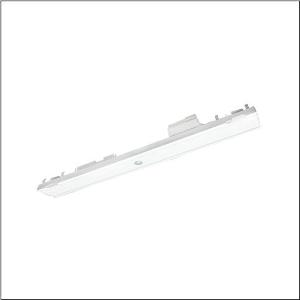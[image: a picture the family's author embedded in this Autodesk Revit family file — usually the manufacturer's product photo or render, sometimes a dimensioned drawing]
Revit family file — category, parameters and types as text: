
# Revit family: licross_r_56tl157c4x31_efa4
name_source: partatom
category: Lighting Fixtures
units: mm (PartAtom-declared; Revit-internal decimal feet)

## family parameters
Cut with Voids When Loaded = No
Host = Face
Light Source = No
Part Type = Normal
Room Calculation Point = No
Round Connector Dimension = Use Diameter
Shared = No

## types (1)
- Licross® (1 x LED, 320 lm, 3.9 W, 4000K)
    Apparent Load = 4 VA
    CIE Flux Codes = 31 68 99 100 100
    Color Rendering = 70
    Color Temperature = 4000K
    Default Elevation = 1800 mm
    Description = Licross®, luminaire insert, of sheet steel, coil coated, white, length: 500mm, width: 59mm, height: 60mm, mounting height: 2.5..7m, emergency light element,LED rated luminous flux: 320lm, light colour: 740, control gear: CEAG, with plug, 6-pole, with phase selection, mains connection: 220..240V, AC/DC, 0/50..60Hz, rated input power: 3.9W, halogen-free wiring, for trunking rail, 9..14-pole, for emergency light function, supply monitoring module CEAG, with address switch, choice between two emergency light lines via tool-free moving of contact pin prior to installation in trunking rail, primary light control with lens, of PMMA, primary optical cover: cover, of PMMA, light emission: direct distribution, primary light characteristic: symmetric,  for area, compatible with all CEAG STAR technology systems (ZB-S, DG-S (DualGuard-S), LP-STAR, AT-S+), protection rating (complete): IP40, insulation class (complete): insulation class I (protective earthing), certification: CE, UKCA, protection symbol: D if used in an environment without relevant dust loads, impact resistance: IK06, permissible ambient temperature for indoor applications: -20..+40°C, packaging unit: 1 piece
    Height = 60 mm  [stored 0.19685 ft]
    Lamp = 1 x LED
    Lamp Light Flux = 320 lm
    Lamp Power = 3.9 W
    Lamp count = 1
    Length = 500 mm
    Luminous efficacy = 82 lm/W
    Manufacturer = Siteco
    ModVariant = No
    Model = 56TL157C4X31
    Mounting Place = Ceiling
    Mounting Type = Pendant
    Number of Poles = 1
    OnlyDefault = Yes
    Power Factor = 1
    Product Name = Licross®
    Product group = luminaire insert
    ProductGroupID = 901
    Protection Class = Protection class I
    Protection Degree = IP 40
    RLX_Detail_Level = 1
    RLX_Emergency_Light_Flux = 0 lm
    RLX_Emergency_Type = 0
    RLX_Emergency_Type_DB = No
    RlxData = <blob elided: 14329 chars, md5=3622ab49>
    Socket = socket
    Standby Power = 0 W
    System Light Flux = 320 lm
    System Power = 4 W
    Type Comments = Product without accessories
    Type Image = l_1251804.jpg
    URL = http://relux.com
    VarID = ---
    Voltage = 0 V
    Weight = 0.00 kg
    Width = 59 mm

note: [stored X ft] marks values corroborated as IEEE doubles in the binary element streams (Revit-internal decimal feet)

## geometry (parser evidence)
native form markers: Sweep x11
no freeform markers — native parametric forms only
